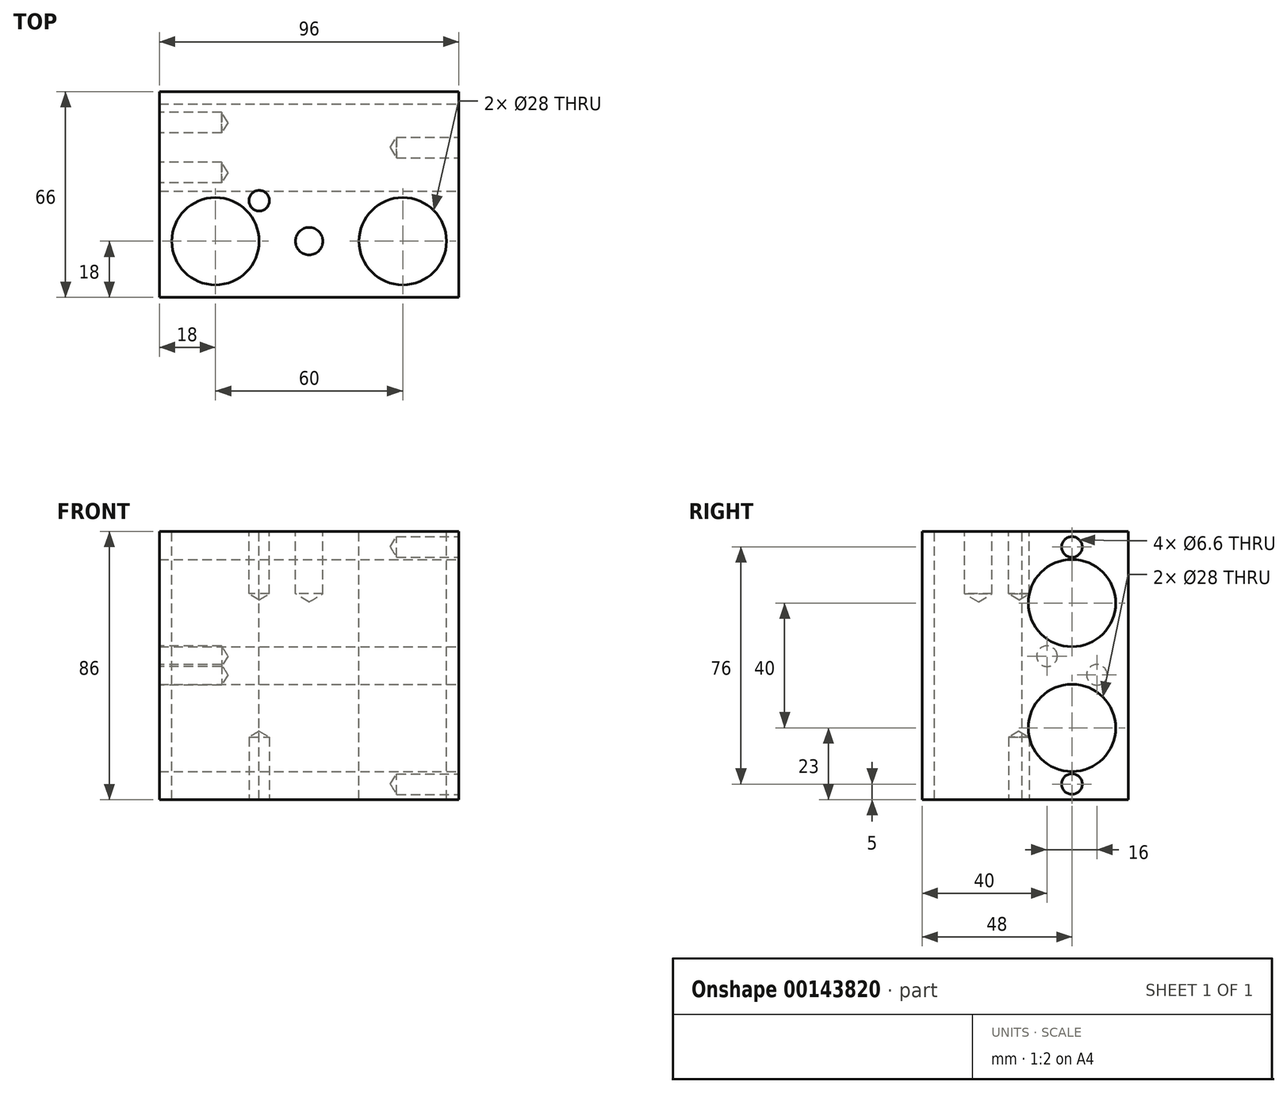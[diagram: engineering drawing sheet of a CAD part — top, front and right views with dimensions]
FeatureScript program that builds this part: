
annotation { "Feature Type Name" : "Feature", "Feature Type Description" : "" }
export const myFeature = defineFeature(function(context is Context, id is Id, definition is map)
    precondition{}
    {
        {
            var Q0;
            Q0=qCreatedBy(makeId("Front.planeOp"),FACE);
            var sketch = newSketch(context, id + "F0", { "sketchPlane" : qUnion([Q0])});
            skLineSegment(sketch, "E0.bottom", {"start": v(0, 0) * mm, "end": v(96, 0) * mm});
            skLineSegment(sketch, "E0.top", {"start": v(0, -86) * mm, "end": v(96, -86) * mm});
            skLineSegment(sketch, "E0.left", {"start": v(0, 0) * mm, "end": v(0, -86) * mm});
            skLineSegment(sketch, "E0.right", {"start": v(96, 0) * mm, "end": v(96, -86) * mm});
            skSolve(sketch);
        }
        {
            var Q0;
            Q0=makeQuery(id+"F0.imprint","IMPRINT",FACE,{"disambiguationData":[TD([[makeQuery(id+"F0.imprint","IMPRINT",EDGE,{"derivedFrom":sQuery(id+"F0.wireOp",EDGE,"E0.bottom")}),-1.0]])]});
            extrude(context, id + "F1", {"entities" : qUnion([Q0]), "oppositeDirection" : true, "depth" : 66 * mm});
        }
        {
            var Q0;
            Q0=makeQuery(id+"F1.opExtrude","SWEPT_FACE",FACE,{"disambiguationData":[OSD([sQuery(id+"F0.wireOp",EDGE,"E0.bottom")])]});
            var sketch = newSketch(context, id + "F2", { "sketchPlane" : qUnion([Q0])});
            skCircle(sketch, "E1", {"center": v(78, 18) * mm, "radius": 14 * mm});
            skCircle(sketch, "E2", {"center": v(18, 18) * mm, "radius": 14 * mm});
            skSolve(sketch);
        }
        {
            var Q0;
            Q0=sQuery(id+"F2.wireOp",VERTEX,"E2.center");
            var Q1;
            Q1=sQuery(id+"F2.wireOp",VERTEX,"E1.center");
            var Q2;
            Q2=makeQuery(id+"F1.opExtrude","SWEPT_BODY",BODY,{"disambiguationData":[OSD([sQuery(id+"F0.wireOp",EDGE,"E0.bottom"),sQuery(id+"F0.wireOp",EDGE,"E0.top"),sQuery(id+"F0.wireOp",EDGE,"E0.left"),sQuery(id+"F0.wireOp",EDGE,"E0.right")])]});
            hole(context, id + "F3", {"style" : HoleStyle.SIMPLE, "endStyle" : HoleEndStyle.THROUGH, "holeDiameter" : 28 * mm, "locations" : qUnion([Q0, Q1]), "scope" : qUnion([Q2]), "isTappedThrough" : true});
        }
        {
            var Q0;
            Q0=makeQuery(id+"F1.opExtrude","SWEPT_FACE",FACE,{"disambiguationData":[OSD([sQuery(id+"F0.wireOp",EDGE,"E0.right")])]});
            var sketch = newSketch(context, id + "F4", { "sketchPlane" : qUnion([Q0])});
            skCircle(sketch, "E3", {"center": v(48, -23) * mm, "radius": 14 * mm});
            skCircle(sketch, "E4", {"center": v(48, -63) * mm, "radius": 14 * mm});
            skSolve(sketch);
        }
        {
            var Q0;
            Q0=sQuery(id+"F4.wireOp",VERTEX,"E3.center");
            var Q1;
            Q1=sQuery(id+"F4.wireOp",VERTEX,"E4.center");
            var Q2;
            Q2=makeQuery(id+"F1.opExtrude","SWEPT_BODY",BODY,{"disambiguationData":[OSD([sQuery(id+"F0.wireOp",EDGE,"E0.bottom"),sQuery(id+"F0.wireOp",EDGE,"E0.top"),sQuery(id+"F0.wireOp",EDGE,"E0.left"),sQuery(id+"F0.wireOp",EDGE,"E0.right")])]});
            hole(context, id + "F5", {"style" : HoleStyle.SIMPLE, "endStyle" : HoleEndStyle.THROUGH, "holeDiameter" : 28 * mm, "locations" : qUnion([Q0, Q1]), "scope" : qUnion([Q2]), "isTappedThrough" : true});
        }
        {
            var Q0;
            Q0=makeQuery(id+"F1.opExtrude","SWEPT_FACE",FACE,{"disambiguationData":[OSD([sQuery(id+"F0.wireOp",EDGE,"E0.bottom")])]});
            var sketch = newSketch(context, id + "F6", { "sketchPlane" : qUnion([Q0])});
            skCircle(sketch, "E5", {"center": v(48, 18) * mm, "radius": 3.4 * mm});
            skSolve(sketch);
        }
        {
            var Q0;
            Q0=sQuery(id+"F6.wireOp",VERTEX,"E5.center");
            var Q1;
            Q1=makeQuery(id+"F1.opExtrude","SWEPT_BODY",BODY,{"disambiguationData":[OSD([sQuery(id+"F0.wireOp",EDGE,"E0.bottom"),sQuery(id+"F0.wireOp",EDGE,"E0.top"),sQuery(id+"F0.wireOp",EDGE,"E0.left"),sQuery(id+"F0.wireOp",EDGE,"E0.right")])]});
            hole(context, id + "F7", {"style" : HoleStyle.SIMPLE, "endStyle" : HoleEndStyle.BLIND, "standardTappedOrClearance" : lookupTablePath({ "standard" : "ISO", "fit" : "Normal", "size" : "M8", "type" : "Clearance" }), "standardBlindInLast" : lookupTablePath({ "fit" : "Standard", "standard" : "ISO", "size" : "M8", "type" : "Clearance" }), "holeDiameter" : 8.8 * mm, "holeDepth" : 20 * mm, "startFromSketch" : true, "locations" : qUnion([Q0]), "scope" : qUnion([Q1])});
        }
        {
            var Q0;
            Q0=makeQuery(id+"F1.opExtrude","SWEPT_FACE",FACE,{"disambiguationData":[OSD([sQuery(id+"F0.wireOp",EDGE,"E0.bottom")])]});
            var sketch = newSketch(context, id + "F8", { "sketchPlane" : qUnion([Q0])});
            skCircle(sketch, "E6", {"center": v(32, 31) * mm, "radius": 2.1 * mm});
            skSolve(sketch);
        }
        {
            var Q0;
            Q0=sQuery(id+"F8.wireOp",VERTEX,"E6.center");
            var Q1;
            Q1=makeQuery(id+"F1.opExtrude","SWEPT_BODY",BODY,{"disambiguationData":[OSD([sQuery(id+"F0.wireOp",EDGE,"E0.bottom"),sQuery(id+"F0.wireOp",EDGE,"E0.top"),sQuery(id+"F0.wireOp",EDGE,"E0.left"),sQuery(id+"F0.wireOp",EDGE,"E0.right")])]});
            hole(context, id + "F9", {"style" : HoleStyle.SIMPLE, "endStyle" : HoleEndStyle.BLIND, "standardTappedOrClearance" : lookupTablePath({ "standard" : "ISO", "fit" : "Normal", "size" : "M6", "type" : "Clearance" }), "standardBlindInLast" : lookupTablePath({ "fit" : "Standard", "standard" : "ISO", "size" : "M6", "type" : "Clearance" }), "holeDiameter" : 6.6 * mm, "holeDepth" : 20 * mm, "startFromSketch" : true, "locations" : qUnion([Q0]), "scope" : qUnion([Q1])});
        }
        {
            var Q0;
            Q0=makeQuery(id+"F1.opExtrude","SWEPT_FACE",FACE,{"disambiguationData":[OSD([sQuery(id+"F0.wireOp",EDGE,"E0.right")])]});
            var sketch = newSketch(context, id + "F10", { "sketchPlane" : qUnion([Q0])});
            skCircle(sketch, "E7", {"center": v(48, -81) * mm, "radius": 0.92 * mm});
            skCircle(sketch, "E8", {"center": v(48, -5) * mm, "radius": 1.2 * mm});
            skSolve(sketch);
        }
        {
            var Q0;
            Q0=sQuery(id+"F10.wireOp",VERTEX,"E7.center");
            var Q1;
            Q1=sQuery(id+"F10.wireOp",VERTEX,"E8.center");
            var Q2;
            Q2=makeQuery(id+"F1.opExtrude","SWEPT_BODY",BODY,{"disambiguationData":[OSD([sQuery(id+"F0.wireOp",EDGE,"E0.bottom"),sQuery(id+"F0.wireOp",EDGE,"E0.top"),sQuery(id+"F0.wireOp",EDGE,"E0.left"),sQuery(id+"F0.wireOp",EDGE,"E0.right")])]});
            hole(context, id + "F11", {"style" : HoleStyle.SIMPLE, "endStyle" : HoleEndStyle.BLIND, "standardTappedOrClearance" : lookupTablePath({ "standard" : "ISO", "fit" : "Normal", "size" : "M6", "type" : "Clearance" }), "standardBlindInLast" : lookupTablePath({ "fit" : "Standard", "standard" : "ISO", "size" : "M6", "type" : "Clearance" }), "holeDiameter" : 6.6 * mm, "holeDepth" : 20 * mm, "startFromSketch" : true, "locations" : qUnion([Q0, Q1]), "scope" : qUnion([Q2])});
        }
        {
            var Q0;
            Q0=makeQuery(id+"F1.opExtrude","SWEPT_FACE",FACE,{"disambiguationData":[OSD([sQuery(id+"F0.wireOp",EDGE,"E0.top")])]});
            var sketch = newSketch(context, id + "F12", { "sketchPlane" : qUnion([Q0])});
            skCircle(sketch, "E9", {"center": v(32, -31) * mm, "radius": 2.64 * mm});
            skSolve(sketch);
        }
        {
            var Q0;
            Q0=sQuery(id+"F12.wireOp",VERTEX,"E9.center");
            var Q1;
            Q1=makeQuery(id+"F1.opExtrude","SWEPT_BODY",BODY,{"disambiguationData":[OSD([sQuery(id+"F0.wireOp",EDGE,"E0.bottom"),sQuery(id+"F0.wireOp",EDGE,"E0.top"),sQuery(id+"F0.wireOp",EDGE,"E0.left"),sQuery(id+"F0.wireOp",EDGE,"E0.right")])]});
            hole(context, id + "F13", {"style" : HoleStyle.SIMPLE, "endStyle" : HoleEndStyle.BLIND, "standardTappedOrClearance" : lookupTablePath({ "standard" : "ISO", "fit" : "Normal", "size" : "M6", "type" : "Clearance" }), "standardBlindInLast" : lookupTablePath({ "fit" : "Standard", "standard" : "ISO", "size" : "M6", "type" : "Clearance" }), "holeDiameter" : 6.6 * mm, "holeDepth" : 20 * mm, "startFromSketch" : true, "locations" : qUnion([Q0]), "scope" : qUnion([Q1])});
        }
        {
            var Q0;
            Q0=makeQuery(id+"F1.opExtrude","SWEPT_FACE",FACE,{"disambiguationData":[OSD([sQuery(id+"F0.wireOp",EDGE,"E0.left")])]});
            var sketch = newSketch(context, id + "F14", { "sketchPlane" : qUnion([Q0])});
            skCircle(sketch, "E10", {"center": v(-56, -46) * mm, "radius": 2.53 * mm});
            skCircle(sketch, "E11", {"center": v(-40, -40) * mm, "radius": 2.02 * mm});
            skSolve(sketch);
        }
        {
            var Q0;
            Q0=sQuery(id+"F14.wireOp",VERTEX,"E10.center");
            var Q1;
            Q1=sQuery(id+"F14.wireOp",VERTEX,"E11.center");
            var Q2;
            Q2=makeQuery(id+"F1.opExtrude","SWEPT_BODY",BODY,{"disambiguationData":[OSD([sQuery(id+"F0.wireOp",EDGE,"E0.bottom"),sQuery(id+"F0.wireOp",EDGE,"E0.top"),sQuery(id+"F0.wireOp",EDGE,"E0.left"),sQuery(id+"F0.wireOp",EDGE,"E0.right")])]});
            hole(context, id + "F15", {"style" : HoleStyle.SIMPLE, "endStyle" : HoleEndStyle.BLIND, "standardTappedOrClearance" : lookupTablePath({ "standard" : "ISO", "fit" : "Normal", "size" : "M6", "type" : "Clearance" }), "standardBlindInLast" : lookupTablePath({ "fit" : "Standard", "standard" : "ISO", "size" : "M6", "type" : "Clearance" }), "holeDiameter" : 6.6 * mm, "holeDepth" : 20 * mm, "startFromSketch" : true, "locations" : qUnion([Q0, Q1]), "scope" : qUnion([Q2])});
        }
    });
